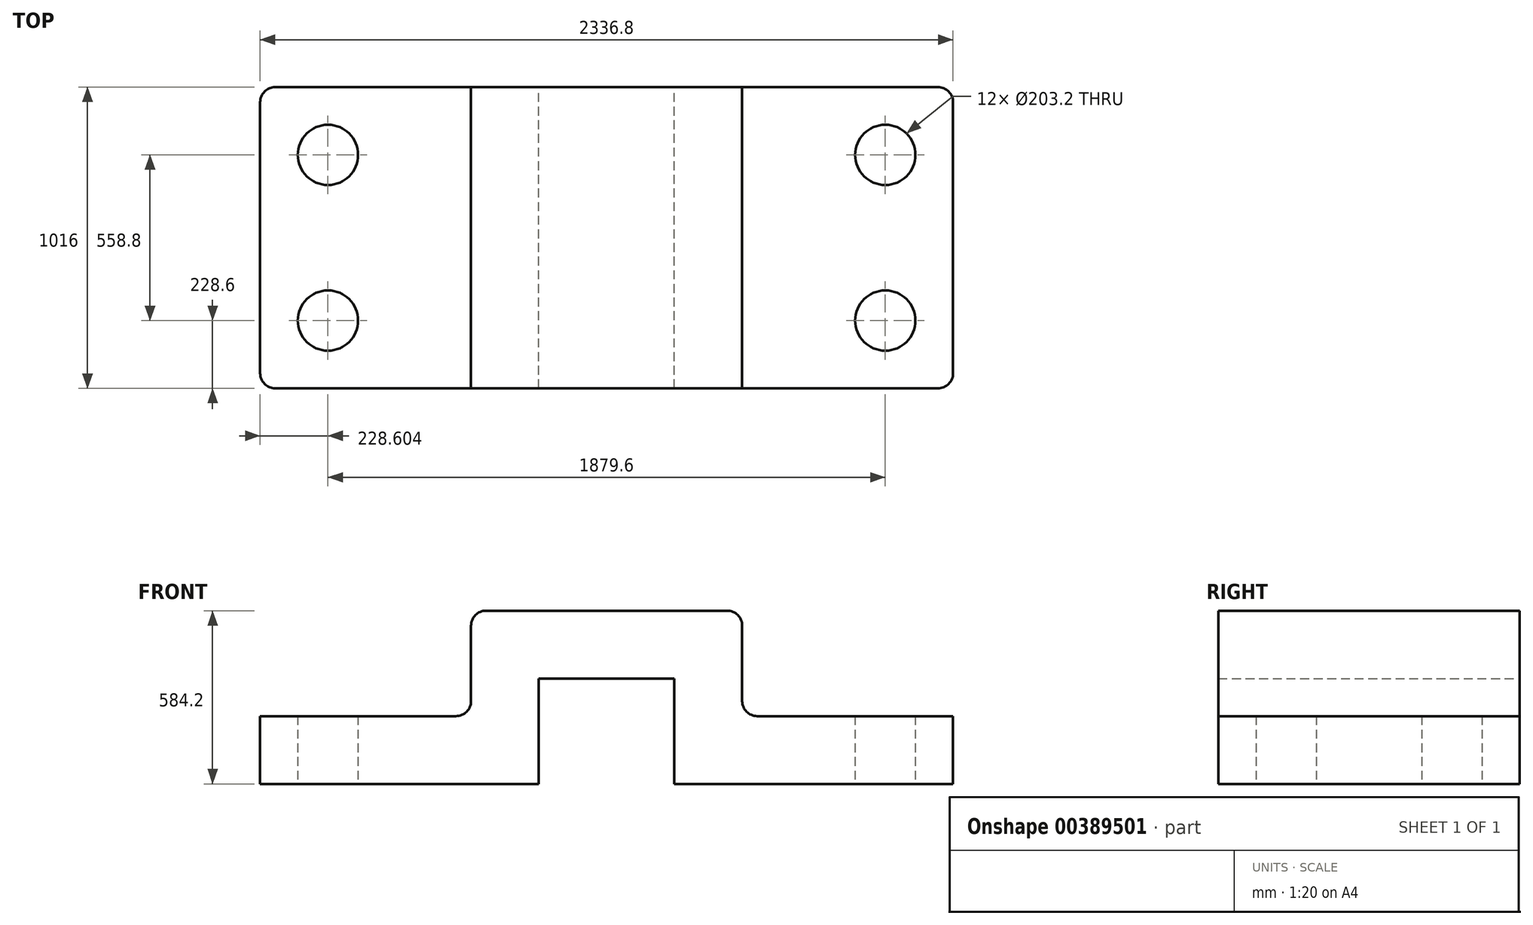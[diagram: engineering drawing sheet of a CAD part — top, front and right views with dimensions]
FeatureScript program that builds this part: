
annotation { "Feature Type Name" : "Feature", "Feature Type Description" : "" }
export const myFeature = defineFeature(function(context is Context, id is Id, definition is map)
    precondition{}
    {
        {
            var Q0;
            Q0=qCreatedBy(makeId("Front.planeOp"),FACE);
            var sketch = newSketch(context, id + "F0", { "sketchPlane" : qUnion([Q0])});
            skLineSegment(sketch, "E0", {"start": v(-1270.84, 0) * mm, "end": v(-331.04, 0) * mm});
            skLineSegment(sketch, "E1", {"start": v(-331.04, 0) * mm, "end": v(-331.04, 355.6) * mm});
            skLineSegment(sketch, "E2", {"start": v(-331.04, 355.6) * mm, "end": v(126.16, 355.6) * mm});
            skLineSegment(sketch, "E3", {"start": v(126.16, 355.6) * mm, "end": v(126.16, 0) * mm});
            skLineSegment(sketch, "E4", {"start": v(126.16, 0) * mm, "end": v(1065.96, 0) * mm});
            skLineSegment(sketch, "E5", {"start": v(1065.96, 0) * mm, "end": v(1065.96, 228.6) * mm});
            skLineSegment(sketch, "E6", {"start": v(1065.96, 228.6) * mm, "end": v(354.76, 228.6) * mm});
            skLineSegment(sketch, "E7", {"start": v(354.76, 228.6) * mm, "end": v(354.76, 584.2) * mm});
            skLineSegment(sketch, "E8", {"start": v(354.76, 584.2) * mm, "end": v(-559.64, 584.2) * mm});
            skLineSegment(sketch, "E9", {"start": v(-559.64, 584.2) * mm, "end": v(-559.64, 228.6) * mm});
            skLineSegment(sketch, "E10", {"start": v(-559.64, 228.6) * mm, "end": v(-1270.84, 228.6) * mm});
            skLineSegment(sketch, "E11", {"start": v(-1270.84, 228.6) * mm, "end": v(-1270.84, 0) * mm});
            skSolve(sketch);
        }
        {
            var Q0;
            Q0=makeQuery(id+"F0.imprint","IMPRINT",FACE,{"disambiguationData":[TD([[makeQuery(id+"F0.imprint","IMPRINT",EDGE,{"derivedFrom":sQuery(id+"F0.wireOp",EDGE,"E0")}),1.0]])]});
            var Q1;
            Q1 = qSketchRegion(id + "F4", true);
            extrude(context, id + "F1", {"entities" : qUnion([Q0, Q1]), "depth" : 1016 * mm});
        }
        {
            var Q0;
            Q0=makeQuery(id+"F1.opExtrude","SWEPT_EDGE",EDGE,{"disambiguationData":[OSD([sQuery(id+"F0.wireOp",EDGE,"E8"),sQuery(id+"F0.wireOp",EDGE,"E9")])]});
            var Q1;
            Q1=makeQuery(id+"F1.opExtrude","SWEPT_EDGE",EDGE,{"disambiguationData":[OSD([sQuery(id+"F0.wireOp",EDGE,"E7"),sQuery(id+"F0.wireOp",EDGE,"E8")])]});
            var Q2;
            Q2=makeQuery(id+"F1.opExtrude","CAP_EDGE",EDGE,{"disambiguationData":[OSD([sQuery(id+"F0.wireOp",EDGE,"E11")])],"isStart":false});
            var Q3;
            Q3=makeQuery(id+"F1.opExtrude","CAP_EDGE",EDGE,{"disambiguationData":[OSD([sQuery(id+"F0.wireOp",EDGE,"E5")])],"isStart":false});
            var Q4;
            Q4=makeQuery(id+"F1.opExtrude","CAP_EDGE",EDGE,{"disambiguationData":[OSD([sQuery(id+"F0.wireOp",EDGE,"E5")])],"isStart":true});
            var Q5;
            Q5=makeQuery(id+"F1.opExtrude","CAP_EDGE",EDGE,{"disambiguationData":[OSD([sQuery(id+"F0.wireOp",EDGE,"E11")])],"isStart":true});
            fillet(context, id + "F2", {"entities" : qUnion([Q0, Q1, Q2, Q3, Q4, Q5]), "radius" : 50.8 * mm, "tangentPropagation" : true, "allowEdgeOverflow" : false});
        }
        {
            var Q0;
            Q0=makeQuery(id+"F1.opExtrude","SWEPT_EDGE",EDGE,{"disambiguationData":[OSD([sQuery(id+"F0.wireOp",EDGE,"E6"),sQuery(id+"F0.wireOp",EDGE,"E7")])]});
            var Q1;
            Q1=makeQuery(id+"F1.opExtrude","SWEPT_EDGE",EDGE,{"disambiguationData":[OSD([sQuery(id+"F0.wireOp",EDGE,"E9"),sQuery(id+"F0.wireOp",EDGE,"E10")])]});
            fillet(context, id + "F3", {"entities" : qUnion([Q0, Q1]), "radius" : 50.8 * mm, "tangentPropagation" : true, "allowEdgeOverflow" : false});
        }
        {
            var Q0;
            Q0=makeQuery(id+"F1.opExtrude","SWEPT_FACE",FACE,{"disambiguationData":[OSD([sQuery(id+"F0.wireOp",EDGE,"E4")])]});
            var sketch = newSketch(context, id + "F4", { "sketchPlane" : qUnion([Q0])});
            skCircle(sketch, "E12", {"center": v(837.36, 787.4) * mm, "radius": 101.6 * mm});
            skCircle(sketch, "E13", {"center": v(837.36, 228.6) * mm, "radius": 101.6 * mm});
            skCircle(sketch, "E14", {"center": v(-1042.24, 787.4) * mm, "radius": 101.6 * mm});
            skCircle(sketch, "E15", {"center": v(-1042.24, 228.6) * mm, "radius": 101.6 * mm});
            skSolve(sketch);
        }
        {
            var Q0;
            Q0=makeQuery(id+"F4.imprint","IMPRINT",FACE,{"disambiguationData":[TD([[makeQuery(id+"F4.imprint","IMPRINT",EDGE,{"derivedFrom":sQuery(id+"F4.wireOp",EDGE,"E13")}),1.0]])]});
            var Q1;
            Q1=makeQuery(id+"F4.imprint","IMPRINT",FACE,{"disambiguationData":[TD([[makeQuery(id+"F4.imprint","IMPRINT",EDGE,{"derivedFrom":sQuery(id+"F4.wireOp",EDGE,"E12")}),1.0]])]});
            var Q2;
            Q2=makeQuery(id+"F4.imprint","IMPRINT",FACE,{"disambiguationData":[TD([[makeQuery(id+"F4.imprint","IMPRINT",EDGE,{"derivedFrom":sQuery(id+"F4.wireOp",EDGE,"E15")}),1.0]])]});
            var Q3;
            Q3=makeQuery(id+"F4.imprint","IMPRINT",FACE,{"disambiguationData":[TD([[makeQuery(id+"F4.imprint","IMPRINT",EDGE,{"derivedFrom":sQuery(id+"F4.wireOp",EDGE,"E14")}),1.0]])]});
            extrude(context, id + "F5", {"entities" : qUnion([Q0, Q1, Q2, Q3]), "operationType" : NewBodyOperationType.REMOVE, "oppositeDirection" : true, "depth" : 228.6 * mm});
        }
    });
